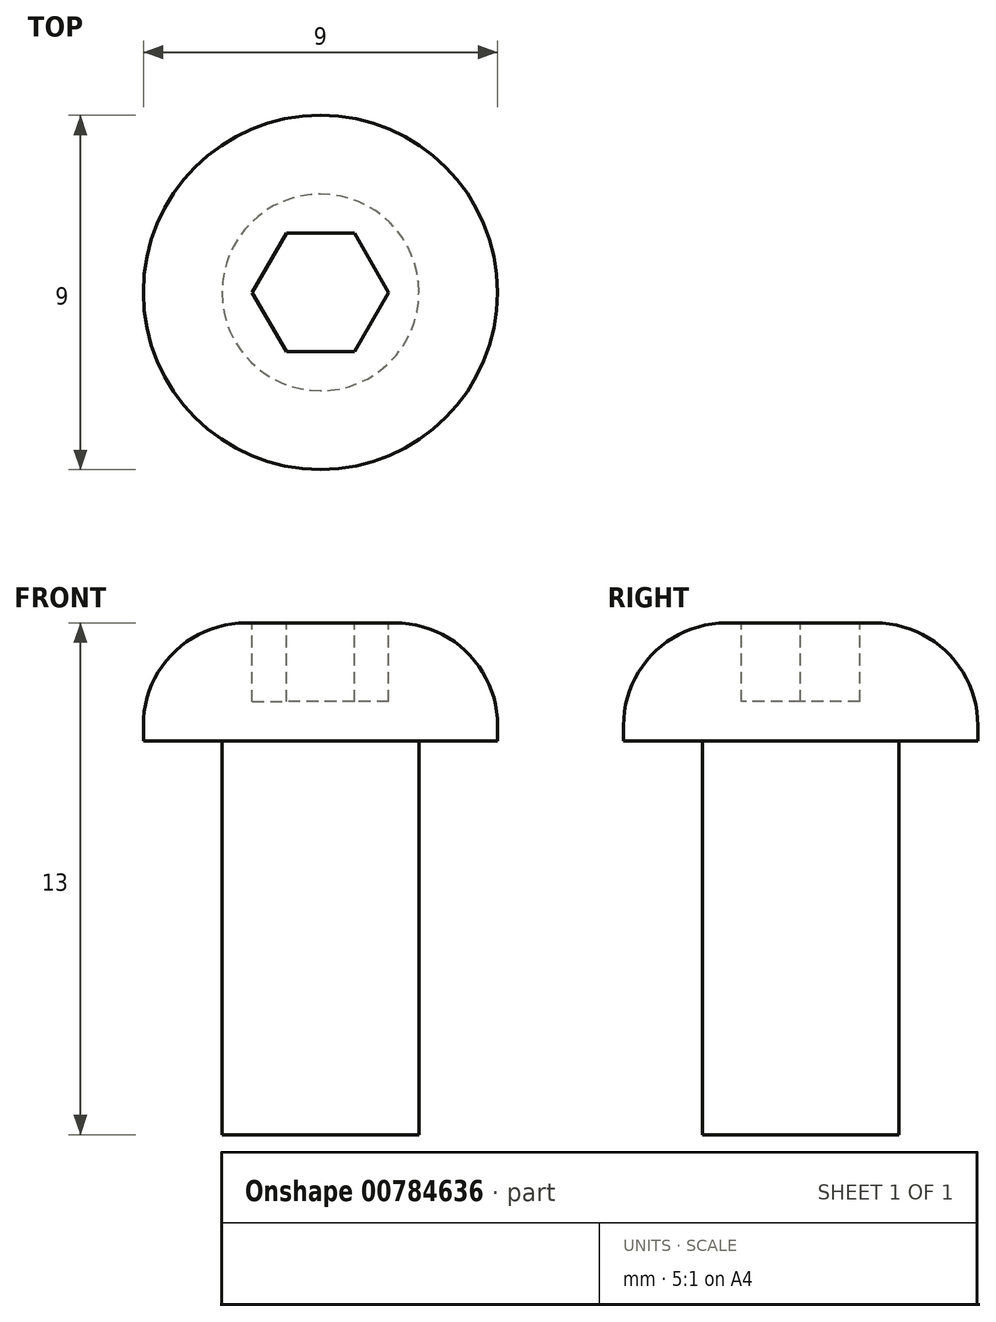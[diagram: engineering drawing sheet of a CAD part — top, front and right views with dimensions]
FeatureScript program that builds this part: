
annotation { "Feature Type Name" : "Feature", "Feature Type Description" : "" }
export const myFeature = defineFeature(function(context is Context, id is Id, definition is map)
    precondition{}
    {
        {
            var Q0;
            Q0=qCreatedBy(makeId("Top.planeOp"),FACE);
            var sketch = newSketch(context, id + "F0", { "sketchPlane" : qUnion([Q0])});
            skCircle(sketch, "E0", {"center": v(0, 0) * mm, "radius": 2.5 * mm});
            skCircle(sketch, "E1", {"center": v(0, 0) * mm, "radius": 4.5 * mm});
            skSolve(sketch);
        }
        {
            var Q0;
            Q0=makeQuery(id+"F0.imprint","IMPRINT",FACE,{"disambiguationData":[TD([[makeQuery(id+"F0.imprint","IMPRINT",EDGE,{"derivedFrom":sQuery(id+"F0.wireOp",EDGE,"E0")}),1.0]])]});
            extrude(context, id + "F1", {"entities" : qUnion([Q0]), "oppositeDirection" : true, "depth" : 10 * mm, "offsetDistance" : 25 * mm});
        }
        {
            var Q0;
            Q0=makeQuery(id+"F0.imprint","IMPRINT",FACE,{"disambiguationData":[TD([[makeQuery(id+"F0.imprint","IMPRINT",EDGE,{"derivedFrom":sQuery(id+"F0.wireOp",EDGE,"E0")}),-1.0]])]});
            var Q1;
            Q1=makeQuery(id+"F0.imprint","IMPRINT",FACE,{"disambiguationData":[TD([[makeQuery(id+"F0.imprint","IMPRINT",EDGE,{"derivedFrom":sQuery(id+"F0.wireOp",EDGE,"E0")}),1.0]])]});
            extrude(context, id + "F2", {"entities" : qUnion([Q0, Q1]), "operationType" : NewBodyOperationType.ADD, "depth" : 3 * mm, "offsetDistance" : 25 * mm});
        }
        {
            var Q0;
            Q0=makeQuery(id+"F2.opExtrude","CAP_EDGE",EDGE,{"disambiguationData":[OSD([sQuery(id+"F0.wireOp",EDGE,"E1")])],"isStart":false});
            fillet(context, id + "F3", {"entities" : qUnion([Q0]), "tangentPropagation" : true, "radius" : 2.6 * mm, "defaultsChanged" : true, "vertexSettings" : [], "allowEdgeOverflow" : false});
        }
        {
            var Q0;
            Q0=makeQuery(id+"F2.opExtrude","CAP_FACE",FACE,{"disambiguationData":[OSD([sQuery(id+"F0.wireOp",EDGE,"E1")])],"isStart":false});
            var sketch = newSketch(context, id + "F4", { "sketchPlane" : qUnion([Q0])});
            skCircle(sketch, "E2.cCircle", {"center": v(0, 0) * mm, "radius": 1.5 * mm, "construction": true});
            skLineSegment(sketch, "E2.0", {"start": v(0.87, -1.5) * mm, "end": v(-0.87, -1.5) * mm});
            skLineSegment(sketch, "E2.1", {"start": v(-0.87, -1.5) * mm, "end": v(-1.73, 0) * mm});
            skLineSegment(sketch, "E2.2", {"start": v(-1.73, 0) * mm, "end": v(-0.87, 1.5) * mm});
            skLineSegment(sketch, "E2.3", {"start": v(-0.87, 1.5) * mm, "end": v(0.87, 1.5) * mm});
            skLineSegment(sketch, "E2.4", {"start": v(0.87, 1.5) * mm, "end": v(1.73, 0) * mm});
            skLineSegment(sketch, "E2.5", {"start": v(1.73, 0) * mm, "end": v(0.87, -1.5) * mm});
            skPoint(sketch, "E2.0.midPoint", {"position": v(0, -1.5) * mm});
            skSolve(sketch);
        }
        {
            var Q0;
            Q0 = qSketchRegion(id + "F4", true);
            extrude(context, id + "F5", {"entities" : qUnion([Q0]), "operationType" : NewBodyOperationType.REMOVE, "oppositeDirection" : true, "depth" : 2 * mm, "offsetDistance" : 25 * mm});
        }
    });
